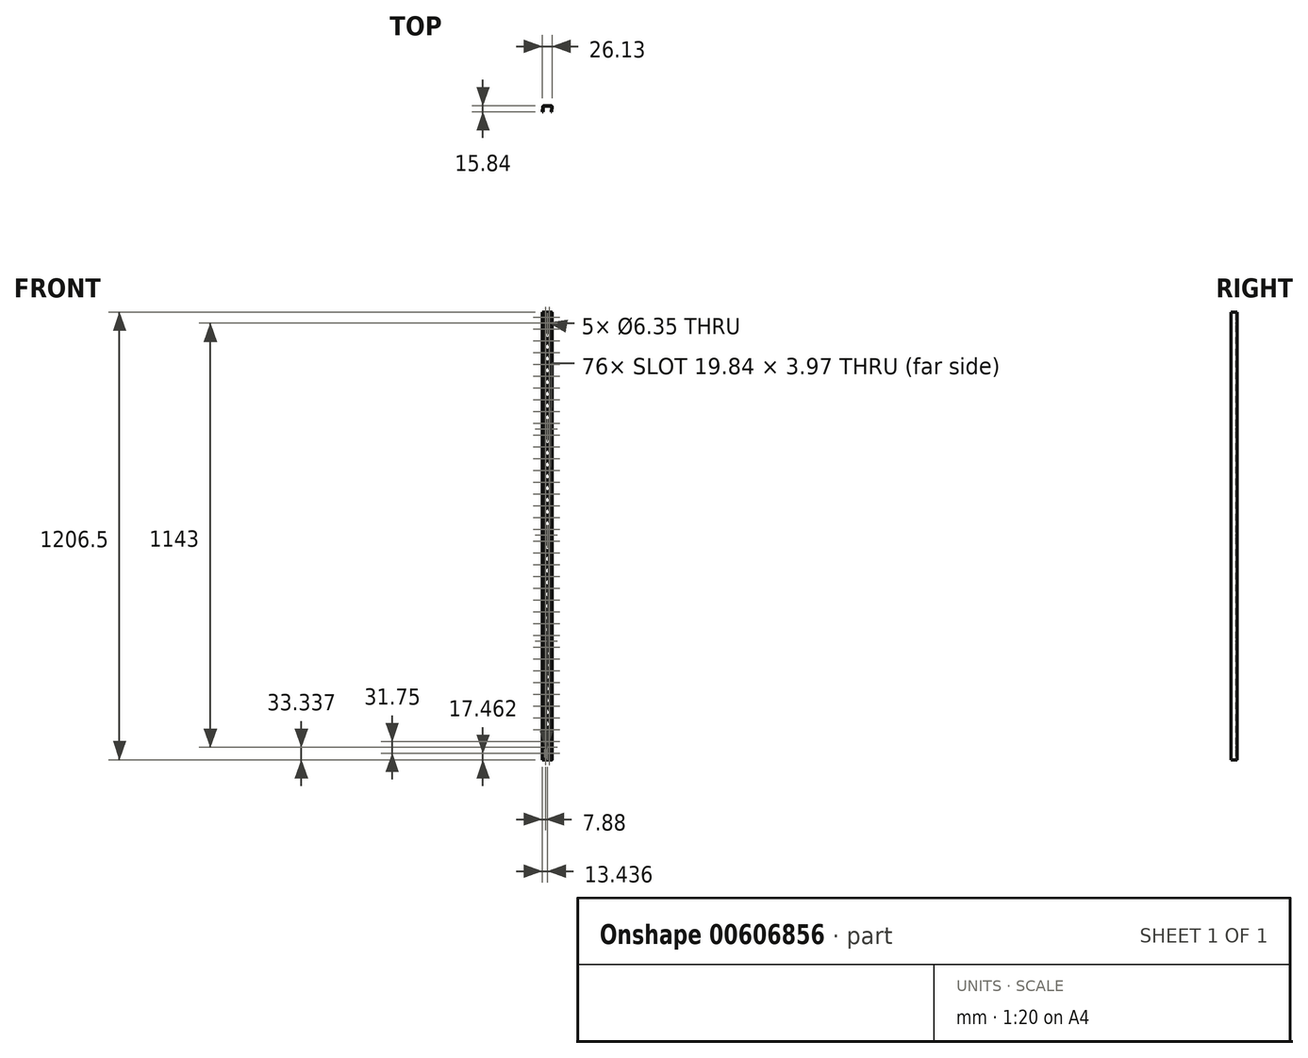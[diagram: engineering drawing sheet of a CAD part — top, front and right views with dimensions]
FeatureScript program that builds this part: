
annotation { "Feature Type Name" : "Feature", "Feature Type Description" : "" }
export const myFeature = defineFeature(function(context is Context, id is Id, definition is map)
    precondition{}
    {
        {
            var Q0;
            Q0=qCreatedBy(makeId("Top.planeOp"),FACE);
            var sketch = newSketch(context, id + "F0", { "sketchPlane" : qUnion([Q0])});
            skLineSegment(sketch, "E0.bottom", {"start": v(9.77, 7.92) * mm, "end": v(-9.22, 7.92) * mm});
            skLineSegment(sketch, "E0.left", {"start": v(12.97, 4.54) * mm, "end": v(12.24, -7.92) * mm});
            skLineSegment(sketch, "E0.right", {"start": v(-12.41, 4.91) * mm, "end": v(-13.16, -7.92) * mm});
            skPoint(sketch, "E0.middle", {"position": v(0, 0) * mm});
            skLineSegment(sketch, "E1.0", {"start": v(11.38, 4.64) * mm, "end": v(10.65, -7.92) * mm});
            skLineSegment(sketch, "E1.1", {"start": v(9.78, 6.34) * mm, "end": v(-9.23, 6.34) * mm});
            skLineSegment(sketch, "E1.2", {"start": v(-10.83, 4.83) * mm, "end": v(-11.57, -7.92) * mm});
            skPoint(sketch, "E2.visualSharp", {"position": v(-10.74, 6.34) * mm});
            skArc(sketch, "E2.filletArc", {"start": v(-9.23, 6.34) * mm, "mid": v(-10.33, 5.9) * mm, "end": v(-10.83, 4.83) * mm});
            skPoint(sketch, "E3.visualSharp", {"position": v(11.48, 6.34) * mm});
            skArc(sketch, "E3.filletArc", {"start": v(11.38, 4.64) * mm, "mid": v(10.95, 5.83) * mm, "end": v(9.78, 6.34) * mm});
            skLineSegment(sketch, "E4", {"start": v(10.65, -7.92) * mm, "end": v(12.24, -7.92) * mm});
            skPoint(sketch, "E5.visualSharp", {"position": v(-12.24, 7.92) * mm});
            skArc(sketch, "E5.filletArc", {"start": v(-9.22, 7.92) * mm, "mid": v(-11.41, 7.05) * mm, "end": v(-12.41, 4.91) * mm});
            skPoint(sketch, "E6.visualSharp", {"position": v(13.16, 7.92) * mm});
            skArc(sketch, "E6.filletArc", {"start": v(12.97, 4.54) * mm, "mid": v(12.1, 6.92) * mm, "end": v(9.77, 7.92) * mm});
            skLineSegment(sketch, "E7", {"start": v(-11.57, -7.92) * mm, "end": v(-13.16, -7.92) * mm});
            skSolve(sketch);
        }
        {
            var Q0;
            Q0 = qSketchRegion(id + "F0", true);
            extrude(context, id + "F1", {"entities" : qUnion([Q0]), "depth" : 1206.5 * mm, "offsetDistance" : 25.4 * mm});
        }
        {
            var Q0;
            Q0=makeQuery(id+"F1.opExtrude","SWEPT_FACE",FACE,{"disambiguationData":[OSD([sQuery(id+"F0.wireOp",EDGE,"E0.bottom")])]});
            var sketch = newSketch(context, id + "F2", { "sketchPlane" : qUnion([Q0])});
            skCircle(sketch, "E8", {"center": v(-0.28, 33.34) * mm, "radius": 3.18 * mm});
            skPoint(sketch, "E8.centerSnap0", {"position": v(-0.28, 0) * mm});
            skCircle(sketch, "E9.0.1.0", {"center": v(-0.28, 319.09) * mm, "radius": 3.18 * mm});
            skCircle(sketch, "E9.0.2.0", {"center": v(-0.28, 604.84) * mm, "radius": 3.18 * mm});
            skCircle(sketch, "E9.0.3.0", {"center": v(-0.28, 890.59) * mm, "radius": 3.18 * mm});
            skCircle(sketch, "E9.0.4.0", {"center": v(-0.28, 1176.34) * mm, "radius": 3.18 * mm});
            skLineSegment(sketch, "E9.direction1", {"start": v(-0.28, 33.34) * mm, "end": v(25.12, 33.34) * mm, "construction": true});
            skLineSegment(sketch, "E9.direction2", {"start": v(-0.28, 33.34) * mm, "end": v(-0.28, 319.09) * mm, "construction": true});
            skSolve(sketch);
        }
        {
            var Q0;
            Q0=makeQuery(id+"F2.imprint","IMPRINT",FACE,{"disambiguationData":[TD([[makeQuery(id+"F2.imprint","IMPRINT",EDGE,{"derivedFrom":sQuery(id+"F2.wireOp",EDGE,"E8")}),1.0]])]});
            var Q1;
            Q1=makeQuery(id+"F2.imprint","IMPRINT",FACE,{"disambiguationData":[TD([[makeQuery(id+"F2.imprint","IMPRINT",EDGE,{"derivedFrom":sQuery(id+"F2.wireOp",EDGE,"E9.0.1.0")}),1.0]])]});
            var Q2;
            Q2=makeQuery(id+"F2.imprint","IMPRINT",FACE,{"disambiguationData":[TD([[makeQuery(id+"F2.imprint","IMPRINT",EDGE,{"derivedFrom":sQuery(id+"F2.wireOp",EDGE,"E9.0.2.0")}),1.0]])]});
            var Q3;
            Q3=makeQuery(id+"F2.imprint","IMPRINT",FACE,{"disambiguationData":[TD([[makeQuery(id+"F2.imprint","IMPRINT",EDGE,{"derivedFrom":sQuery(id+"F2.wireOp",EDGE,"E9.0.3.0")}),1.0]])]});
            var Q4;
            Q4=makeQuery(id+"F2.imprint","IMPRINT",FACE,{"disambiguationData":[TD([[makeQuery(id+"F2.imprint","IMPRINT",EDGE,{"derivedFrom":sQuery(id+"F2.wireOp",EDGE,"E9.0.4.0")}),1.0]])]});
            extrude(context, id + "F3", {"entities" : qUnion([Q0, Q1, Q2, Q3, Q4]), "operationType" : NewBodyOperationType.REMOVE, "oppositeDirection" : true, "depth" : 25.4 * mm, "offsetDistance" : 25.4 * mm});
        }
        {
            var Q0;
            Q0=makeQuery(id+"F1.opExtrude","SWEPT_FACE",FACE,{"disambiguationData":[OSD([sQuery(id+"F0.wireOp",EDGE,"E0.bottom")])]});
            var sketch = newSketch(context, id + "F4", { "sketchPlane" : qUnion([Q0])});
            skLineSegment(sketch, "E10", {"start": v(-0.28, 1204.55) * mm, "end": v(-0.28, 1138.18) * mm, "construction": true});
            skPoint(sketch, "E10.startSnap0", {"position": v(-0.28, 1206.5) * mm});
            skLineSegment(sketch, "E11.left", {"start": v(-7.82, 1200.15) * mm, "end": v(-7.82, 1184.27) * mm});
            skLineSegment(sketch, "E11.right", {"start": v(-3.85, 1200.15) * mm, "end": v(-3.85, 1184.27) * mm});
            skArc(sketch, "E12", {"start": v(-3.85, 1200.15) * mm, "mid": v(-5.83, 1202.13) * mm, "end": v(-7.82, 1200.15) * mm});
            skArc(sketch, "E13", {"start": v(-7.82, 1184.27) * mm, "mid": v(-5.83, 1182.3) * mm, "end": v(-3.85, 1184.27) * mm});
            skLineSegment(sketch, "E14.0.1.0", {"start": v(-3.85, 1168.4) * mm, "end": v(-3.85, 1152.53) * mm});
            skArc(sketch, "E14.0.1.1", {"start": v(-7.82, 1152.53) * mm, "mid": v(-5.83, 1150.54) * mm, "end": v(-3.85, 1152.53) * mm});
            skLineSegment(sketch, "E14.0.1.2", {"start": v(-7.82, 1168.4) * mm, "end": v(-7.82, 1152.53) * mm});
            skArc(sketch, "E14.0.1.3", {"start": v(-3.85, 1168.4) * mm, "mid": v(-5.83, 1170.38) * mm, "end": v(-7.82, 1168.4) * mm});
            skLineSegment(sketch, "E14.0.2.0", {"start": v(-3.85, 1136.65) * mm, "end": v(-3.85, 1120.78) * mm});
            skArc(sketch, "E14.0.2.1", {"start": v(-7.82, 1120.78) * mm, "mid": v(-5.83, 1118.8) * mm, "end": v(-3.85, 1120.78) * mm});
            skLineSegment(sketch, "E14.0.2.2", {"start": v(-7.82, 1136.65) * mm, "end": v(-7.82, 1120.78) * mm});
            skArc(sketch, "E14.0.2.3", {"start": v(-3.85, 1136.65) * mm, "mid": v(-5.83, 1138.63) * mm, "end": v(-7.82, 1136.65) * mm});
            skLineSegment(sketch, "E14.0.3.0", {"start": v(-3.85, 1104.9) * mm, "end": v(-3.85, 1089.03) * mm});
            skArc(sketch, "E14.0.3.1", {"start": v(-7.82, 1089.03) * mm, "mid": v(-5.83, 1087.04) * mm, "end": v(-3.85, 1089.03) * mm});
            skLineSegment(sketch, "E14.0.3.2", {"start": v(-7.82, 1104.9) * mm, "end": v(-7.82, 1089.03) * mm});
            skArc(sketch, "E14.0.3.3", {"start": v(-3.85, 1104.9) * mm, "mid": v(-5.83, 1106.88) * mm, "end": v(-7.82, 1104.9) * mm});
            skLineSegment(sketch, "E14.0.4.0", {"start": v(-3.85, 1073.15) * mm, "end": v(-3.85, 1057.28) * mm});
            skArc(sketch, "E14.0.4.1", {"start": v(-7.82, 1057.28) * mm, "mid": v(-5.83, 1055.3) * mm, "end": v(-3.85, 1057.28) * mm});
            skLineSegment(sketch, "E14.0.4.2", {"start": v(-7.82, 1073.15) * mm, "end": v(-7.82, 1057.28) * mm});
            skArc(sketch, "E14.0.4.3", {"start": v(-3.85, 1073.15) * mm, "mid": v(-5.83, 1075.13) * mm, "end": v(-7.82, 1073.15) * mm});
            skLineSegment(sketch, "E14.0.5.0", {"start": v(-3.85, 1041.4) * mm, "end": v(-3.85, 1025.53) * mm});
            skArc(sketch, "E14.0.5.1", {"start": v(-7.82, 1025.53) * mm, "mid": v(-5.83, 1023.54) * mm, "end": v(-3.85, 1025.53) * mm});
            skLineSegment(sketch, "E14.0.5.2", {"start": v(-7.82, 1041.4) * mm, "end": v(-7.82, 1025.53) * mm});
            skArc(sketch, "E14.0.5.3", {"start": v(-3.85, 1041.4) * mm, "mid": v(-5.83, 1043.38) * mm, "end": v(-7.82, 1041.4) * mm});
            skLineSegment(sketch, "E14.0.6.0", {"start": v(-3.85, 1009.65) * mm, "end": v(-3.85, 993.78) * mm});
            skArc(sketch, "E14.0.6.1", {"start": v(-7.82, 993.78) * mm, "mid": v(-5.83, 991.8) * mm, "end": v(-3.85, 993.78) * mm});
            skLineSegment(sketch, "E14.0.6.2", {"start": v(-7.82, 1009.65) * mm, "end": v(-7.82, 993.78) * mm});
            skArc(sketch, "E14.0.6.3", {"start": v(-3.85, 1009.65) * mm, "mid": v(-5.83, 1011.63) * mm, "end": v(-7.82, 1009.65) * mm});
            skLineSegment(sketch, "E14.0.7.0", {"start": v(-3.85, 977.9) * mm, "end": v(-3.85, 962.03) * mm});
            skArc(sketch, "E14.0.7.1", {"start": v(-7.82, 962.03) * mm, "mid": v(-5.83, 960.04) * mm, "end": v(-3.85, 962.03) * mm});
            skLineSegment(sketch, "E14.0.7.2", {"start": v(-7.82, 977.9) * mm, "end": v(-7.82, 962.03) * mm});
            skArc(sketch, "E14.0.7.3", {"start": v(-3.85, 977.9) * mm, "mid": v(-5.83, 979.88) * mm, "end": v(-7.82, 977.9) * mm});
            skLineSegment(sketch, "E14.0.8.0", {"start": v(-3.85, 946.15) * mm, "end": v(-3.85, 930.28) * mm});
            skArc(sketch, "E14.0.8.1", {"start": v(-7.82, 930.28) * mm, "mid": v(-5.83, 928.3) * mm, "end": v(-3.85, 930.28) * mm});
            skLineSegment(sketch, "E14.0.8.2", {"start": v(-7.82, 946.15) * mm, "end": v(-7.82, 930.28) * mm});
            skArc(sketch, "E14.0.8.3", {"start": v(-3.85, 946.15) * mm, "mid": v(-5.83, 948.13) * mm, "end": v(-7.82, 946.15) * mm});
            skLineSegment(sketch, "E14.0.9.0", {"start": v(-3.85, 914.4) * mm, "end": v(-3.85, 898.53) * mm});
            skArc(sketch, "E14.0.9.1", {"start": v(-7.82, 898.53) * mm, "mid": v(-5.83, 896.54) * mm, "end": v(-3.85, 898.53) * mm});
            skLineSegment(sketch, "E14.0.9.2", {"start": v(-7.82, 914.4) * mm, "end": v(-7.82, 898.53) * mm});
            skArc(sketch, "E14.0.9.3", {"start": v(-3.85, 914.4) * mm, "mid": v(-5.83, 916.38) * mm, "end": v(-7.82, 914.4) * mm});
            skLineSegment(sketch, "E14.0.10.0", {"start": v(-3.85, 882.65) * mm, "end": v(-3.85, 866.78) * mm});
            skArc(sketch, "E14.0.10.1", {"start": v(-7.82, 866.78) * mm, "mid": v(-5.83, 864.8) * mm, "end": v(-3.85, 866.78) * mm});
            skLineSegment(sketch, "E14.0.10.2", {"start": v(-7.82, 882.65) * mm, "end": v(-7.82, 866.78) * mm});
            skArc(sketch, "E14.0.10.3", {"start": v(-3.85, 882.65) * mm, "mid": v(-5.83, 884.63) * mm, "end": v(-7.82, 882.65) * mm});
            skLineSegment(sketch, "E14.0.11.0", {"start": v(-3.85, 850.9) * mm, "end": v(-3.85, 835.03) * mm});
            skArc(sketch, "E14.0.11.1", {"start": v(-7.82, 835.03) * mm, "mid": v(-5.83, 833.04) * mm, "end": v(-3.85, 835.03) * mm});
            skLineSegment(sketch, "E14.0.11.2", {"start": v(-7.82, 850.9) * mm, "end": v(-7.82, 835.03) * mm});
            skArc(sketch, "E14.0.11.3", {"start": v(-3.85, 850.9) * mm, "mid": v(-5.83, 852.88) * mm, "end": v(-7.82, 850.9) * mm});
            skLineSegment(sketch, "E14.0.12.0", {"start": v(-3.85, 819.15) * mm, "end": v(-3.85, 803.28) * mm});
            skArc(sketch, "E14.0.12.1", {"start": v(-7.82, 803.28) * mm, "mid": v(-5.83, 801.3) * mm, "end": v(-3.85, 803.28) * mm});
            skLineSegment(sketch, "E14.0.12.2", {"start": v(-7.82, 819.15) * mm, "end": v(-7.82, 803.28) * mm});
            skArc(sketch, "E14.0.12.3", {"start": v(-3.85, 819.15) * mm, "mid": v(-5.83, 821.13) * mm, "end": v(-7.82, 819.15) * mm});
            skLineSegment(sketch, "E14.0.13.0", {"start": v(-3.85, 787.4) * mm, "end": v(-3.85, 771.53) * mm});
            skArc(sketch, "E14.0.13.1", {"start": v(-7.82, 771.53) * mm, "mid": v(-5.83, 769.54) * mm, "end": v(-3.85, 771.53) * mm});
            skLineSegment(sketch, "E14.0.13.2", {"start": v(-7.82, 787.4) * mm, "end": v(-7.82, 771.53) * mm});
            skArc(sketch, "E14.0.13.3", {"start": v(-3.85, 787.4) * mm, "mid": v(-5.83, 789.38) * mm, "end": v(-7.82, 787.4) * mm});
            skLineSegment(sketch, "E14.0.14.0", {"start": v(-3.85, 755.65) * mm, "end": v(-3.85, 739.78) * mm});
            skArc(sketch, "E14.0.14.1", {"start": v(-7.82, 739.78) * mm, "mid": v(-5.83, 737.8) * mm, "end": v(-3.85, 739.78) * mm});
            skLineSegment(sketch, "E14.0.14.2", {"start": v(-7.82, 755.65) * mm, "end": v(-7.82, 739.78) * mm});
            skArc(sketch, "E14.0.14.3", {"start": v(-3.85, 755.65) * mm, "mid": v(-5.83, 757.63) * mm, "end": v(-7.82, 755.65) * mm});
            skLineSegment(sketch, "E14.0.15.0", {"start": v(-3.85, 723.9) * mm, "end": v(-3.85, 708.03) * mm});
            skArc(sketch, "E14.0.15.1", {"start": v(-7.82, 708.03) * mm, "mid": v(-5.83, 706.04) * mm, "end": v(-3.85, 708.03) * mm});
            skLineSegment(sketch, "E14.0.15.2", {"start": v(-7.82, 723.9) * mm, "end": v(-7.82, 708.03) * mm});
            skArc(sketch, "E14.0.15.3", {"start": v(-3.85, 723.9) * mm, "mid": v(-5.83, 725.88) * mm, "end": v(-7.82, 723.9) * mm});
            skLineSegment(sketch, "E14.0.16.0", {"start": v(-3.85, 692.15) * mm, "end": v(-3.85, 676.28) * mm});
            skArc(sketch, "E14.0.16.1", {"start": v(-7.82, 676.28) * mm, "mid": v(-5.83, 674.3) * mm, "end": v(-3.85, 676.28) * mm});
            skLineSegment(sketch, "E14.0.16.2", {"start": v(-7.82, 692.15) * mm, "end": v(-7.82, 676.28) * mm});
            skArc(sketch, "E14.0.16.3", {"start": v(-3.85, 692.15) * mm, "mid": v(-5.83, 694.13) * mm, "end": v(-7.82, 692.15) * mm});
            skLineSegment(sketch, "E14.0.17.0", {"start": v(-3.85, 660.4) * mm, "end": v(-3.85, 644.53) * mm});
            skArc(sketch, "E14.0.17.1", {"start": v(-7.82, 644.53) * mm, "mid": v(-5.83, 642.54) * mm, "end": v(-3.85, 644.53) * mm});
            skLineSegment(sketch, "E14.0.17.2", {"start": v(-7.82, 660.4) * mm, "end": v(-7.82, 644.53) * mm});
            skArc(sketch, "E14.0.17.3", {"start": v(-3.85, 660.4) * mm, "mid": v(-5.83, 662.38) * mm, "end": v(-7.82, 660.4) * mm});
            skLineSegment(sketch, "E14.0.18.0", {"start": v(-3.85, 628.65) * mm, "end": v(-3.85, 612.78) * mm});
            skArc(sketch, "E14.0.18.1", {"start": v(-7.82, 612.78) * mm, "mid": v(-5.83, 610.8) * mm, "end": v(-3.85, 612.78) * mm});
            skLineSegment(sketch, "E14.0.18.2", {"start": v(-7.82, 628.65) * mm, "end": v(-7.82, 612.78) * mm});
            skArc(sketch, "E14.0.18.3", {"start": v(-3.85, 628.65) * mm, "mid": v(-5.83, 630.63) * mm, "end": v(-7.82, 628.65) * mm});
            skLineSegment(sketch, "E14.0.19.0", {"start": v(-3.85, 596.9) * mm, "end": v(-3.85, 581.03) * mm});
            skArc(sketch, "E14.0.19.1", {"start": v(-7.82, 581.03) * mm, "mid": v(-5.83, 579.04) * mm, "end": v(-3.85, 581.03) * mm});
            skLineSegment(sketch, "E14.0.19.2", {"start": v(-7.82, 596.9) * mm, "end": v(-7.82, 581.03) * mm});
            skArc(sketch, "E14.0.19.3", {"start": v(-3.85, 596.9) * mm, "mid": v(-5.83, 598.88) * mm, "end": v(-7.82, 596.9) * mm});
            skLineSegment(sketch, "E14.0.20.0", {"start": v(-3.85, 565.15) * mm, "end": v(-3.85, 549.28) * mm});
            skArc(sketch, "E14.0.20.1", {"start": v(-7.82, 549.28) * mm, "mid": v(-5.83, 547.3) * mm, "end": v(-3.85, 549.28) * mm});
            skLineSegment(sketch, "E14.0.20.2", {"start": v(-7.82, 565.15) * mm, "end": v(-7.82, 549.28) * mm});
            skArc(sketch, "E14.0.20.3", {"start": v(-3.85, 565.15) * mm, "mid": v(-5.83, 567.13) * mm, "end": v(-7.82, 565.15) * mm});
            skLineSegment(sketch, "E14.0.21.0", {"start": v(-3.85, 533.4) * mm, "end": v(-3.85, 517.53) * mm});
            skArc(sketch, "E14.0.21.1", {"start": v(-7.82, 517.53) * mm, "mid": v(-5.83, 515.54) * mm, "end": v(-3.85, 517.53) * mm});
            skLineSegment(sketch, "E14.0.21.2", {"start": v(-7.82, 533.4) * mm, "end": v(-7.82, 517.53) * mm});
            skArc(sketch, "E14.0.21.3", {"start": v(-3.85, 533.4) * mm, "mid": v(-5.83, 535.38) * mm, "end": v(-7.82, 533.4) * mm});
            skLineSegment(sketch, "E14.0.22.0", {"start": v(-3.85, 501.65) * mm, "end": v(-3.85, 485.78) * mm});
            skArc(sketch, "E14.0.22.1", {"start": v(-7.82, 485.78) * mm, "mid": v(-5.83, 483.8) * mm, "end": v(-3.85, 485.78) * mm});
            skLineSegment(sketch, "E14.0.22.2", {"start": v(-7.82, 501.65) * mm, "end": v(-7.82, 485.78) * mm});
            skArc(sketch, "E14.0.22.3", {"start": v(-3.85, 501.65) * mm, "mid": v(-5.83, 503.63) * mm, "end": v(-7.82, 501.65) * mm});
            skLineSegment(sketch, "E14.0.23.0", {"start": v(-3.85, 469.9) * mm, "end": v(-3.85, 454.03) * mm});
            skArc(sketch, "E14.0.23.1", {"start": v(-7.82, 454.03) * mm, "mid": v(-5.83, 452.04) * mm, "end": v(-3.85, 454.03) * mm});
            skLineSegment(sketch, "E14.0.23.2", {"start": v(-7.82, 469.9) * mm, "end": v(-7.82, 454.03) * mm});
            skArc(sketch, "E14.0.23.3", {"start": v(-3.85, 469.9) * mm, "mid": v(-5.83, 471.88) * mm, "end": v(-7.82, 469.9) * mm});
            skLineSegment(sketch, "E14.0.24.0", {"start": v(-3.85, 438.15) * mm, "end": v(-3.85, 422.28) * mm});
            skArc(sketch, "E14.0.24.1", {"start": v(-7.82, 422.28) * mm, "mid": v(-5.83, 420.3) * mm, "end": v(-3.85, 422.28) * mm});
            skLineSegment(sketch, "E14.0.24.2", {"start": v(-7.82, 438.15) * mm, "end": v(-7.82, 422.28) * mm});
            skArc(sketch, "E14.0.24.3", {"start": v(-3.85, 438.15) * mm, "mid": v(-5.83, 440.13) * mm, "end": v(-7.82, 438.15) * mm});
            skLineSegment(sketch, "E14.0.25.0", {"start": v(-3.85, 406.4) * mm, "end": v(-3.85, 390.53) * mm});
            skArc(sketch, "E14.0.25.1", {"start": v(-7.82, 390.53) * mm, "mid": v(-5.83, 388.54) * mm, "end": v(-3.85, 390.53) * mm});
            skLineSegment(sketch, "E14.0.25.2", {"start": v(-7.82, 406.4) * mm, "end": v(-7.82, 390.53) * mm});
            skArc(sketch, "E14.0.25.3", {"start": v(-3.85, 406.4) * mm, "mid": v(-5.83, 408.38) * mm, "end": v(-7.82, 406.4) * mm});
            skLineSegment(sketch, "E14.0.26.0", {"start": v(-3.85, 374.65) * mm, "end": v(-3.85, 358.78) * mm});
            skArc(sketch, "E14.0.26.1", {"start": v(-7.82, 358.78) * mm, "mid": v(-5.83, 356.8) * mm, "end": v(-3.85, 358.78) * mm});
            skLineSegment(sketch, "E14.0.26.2", {"start": v(-7.82, 374.65) * mm, "end": v(-7.82, 358.78) * mm});
            skArc(sketch, "E14.0.26.3", {"start": v(-3.85, 374.65) * mm, "mid": v(-5.83, 376.63) * mm, "end": v(-7.82, 374.65) * mm});
            skLineSegment(sketch, "E14.0.27.0", {"start": v(-3.85, 342.9) * mm, "end": v(-3.85, 327.03) * mm});
            skArc(sketch, "E14.0.27.1", {"start": v(-7.82, 327.03) * mm, "mid": v(-5.83, 325.04) * mm, "end": v(-3.85, 327.03) * mm});
            skLineSegment(sketch, "E14.0.27.2", {"start": v(-7.82, 342.9) * mm, "end": v(-7.82, 327.03) * mm});
            skArc(sketch, "E14.0.27.3", {"start": v(-3.85, 342.9) * mm, "mid": v(-5.83, 344.88) * mm, "end": v(-7.82, 342.9) * mm});
            skLineSegment(sketch, "E14.0.28.0", {"start": v(-3.85, 311.15) * mm, "end": v(-3.85, 295.28) * mm});
            skArc(sketch, "E14.0.28.1", {"start": v(-7.82, 295.28) * mm, "mid": v(-5.83, 293.3) * mm, "end": v(-3.85, 295.28) * mm});
            skLineSegment(sketch, "E14.0.28.2", {"start": v(-7.82, 311.15) * mm, "end": v(-7.82, 295.28) * mm});
            skArc(sketch, "E14.0.28.3", {"start": v(-3.85, 311.15) * mm, "mid": v(-5.83, 313.13) * mm, "end": v(-7.82, 311.15) * mm});
            skLineSegment(sketch, "E14.0.29.0", {"start": v(-3.85, 279.4) * mm, "end": v(-3.85, 263.53) * mm});
            skArc(sketch, "E14.0.29.1", {"start": v(-7.82, 263.53) * mm, "mid": v(-5.83, 261.54) * mm, "end": v(-3.85, 263.53) * mm});
            skLineSegment(sketch, "E14.0.29.2", {"start": v(-7.82, 279.4) * mm, "end": v(-7.82, 263.53) * mm});
            skArc(sketch, "E14.0.29.3", {"start": v(-3.85, 279.4) * mm, "mid": v(-5.83, 281.38) * mm, "end": v(-7.82, 279.4) * mm});
            skLineSegment(sketch, "E14.0.30.0", {"start": v(-3.85, 247.65) * mm, "end": v(-3.85, 231.78) * mm});
            skArc(sketch, "E14.0.30.1", {"start": v(-7.82, 231.78) * mm, "mid": v(-5.83, 229.8) * mm, "end": v(-3.85, 231.78) * mm});
            skLineSegment(sketch, "E14.0.30.2", {"start": v(-7.82, 247.65) * mm, "end": v(-7.82, 231.78) * mm});
            skArc(sketch, "E14.0.30.3", {"start": v(-3.85, 247.65) * mm, "mid": v(-5.83, 249.63) * mm, "end": v(-7.82, 247.65) * mm});
            skLineSegment(sketch, "E14.0.31.0", {"start": v(-3.85, 215.9) * mm, "end": v(-3.85, 200.03) * mm});
            skArc(sketch, "E14.0.31.1", {"start": v(-7.82, 200.03) * mm, "mid": v(-5.83, 198.04) * mm, "end": v(-3.85, 200.03) * mm});
            skLineSegment(sketch, "E14.0.31.2", {"start": v(-7.82, 215.9) * mm, "end": v(-7.82, 200.03) * mm});
            skArc(sketch, "E14.0.31.3", {"start": v(-3.85, 215.9) * mm, "mid": v(-5.83, 217.88) * mm, "end": v(-7.82, 215.9) * mm});
            skLineSegment(sketch, "E14.0.32.0", {"start": v(-3.85, 184.15) * mm, "end": v(-3.85, 168.28) * mm});
            skArc(sketch, "E14.0.32.1", {"start": v(-7.82, 168.28) * mm, "mid": v(-5.83, 166.3) * mm, "end": v(-3.85, 168.28) * mm});
            skLineSegment(sketch, "E14.0.32.2", {"start": v(-7.82, 184.15) * mm, "end": v(-7.82, 168.28) * mm});
            skArc(sketch, "E14.0.32.3", {"start": v(-3.85, 184.15) * mm, "mid": v(-5.83, 186.13) * mm, "end": v(-7.82, 184.15) * mm});
            skLineSegment(sketch, "E14.0.33.0", {"start": v(-3.85, 152.4) * mm, "end": v(-3.85, 136.53) * mm});
            skArc(sketch, "E14.0.33.1", {"start": v(-7.82, 136.53) * mm, "mid": v(-5.83, 134.54) * mm, "end": v(-3.85, 136.53) * mm});
            skLineSegment(sketch, "E14.0.33.2", {"start": v(-7.82, 152.4) * mm, "end": v(-7.82, 136.53) * mm});
            skArc(sketch, "E14.0.33.3", {"start": v(-3.85, 152.4) * mm, "mid": v(-5.83, 154.38) * mm, "end": v(-7.82, 152.4) * mm});
            skLineSegment(sketch, "E14.0.34.0", {"start": v(-3.85, 120.65) * mm, "end": v(-3.85, 104.78) * mm});
            skArc(sketch, "E14.0.34.1", {"start": v(-7.82, 104.78) * mm, "mid": v(-5.83, 102.8) * mm, "end": v(-3.85, 104.78) * mm});
            skLineSegment(sketch, "E14.0.34.2", {"start": v(-7.82, 120.65) * mm, "end": v(-7.82, 104.78) * mm});
            skArc(sketch, "E14.0.34.3", {"start": v(-3.85, 120.65) * mm, "mid": v(-5.83, 122.63) * mm, "end": v(-7.82, 120.65) * mm});
            skLineSegment(sketch, "E14.0.35.0", {"start": v(-3.85, 88.9) * mm, "end": v(-3.85, 73.03) * mm});
            skArc(sketch, "E14.0.35.1", {"start": v(-7.82, 73.03) * mm, "mid": v(-5.83, 71.04) * mm, "end": v(-3.85, 73.03) * mm});
            skLineSegment(sketch, "E14.0.35.2", {"start": v(-7.82, 88.9) * mm, "end": v(-7.82, 73.03) * mm});
            skArc(sketch, "E14.0.35.3", {"start": v(-3.85, 88.9) * mm, "mid": v(-5.83, 90.88) * mm, "end": v(-7.82, 88.9) * mm});
            skLineSegment(sketch, "E14.0.36.0", {"start": v(-3.85, 57.15) * mm, "end": v(-3.85, 41.28) * mm});
            skArc(sketch, "E14.0.36.1", {"start": v(-7.82, 41.28) * mm, "mid": v(-5.83, 39.3) * mm, "end": v(-3.85, 41.28) * mm});
            skLineSegment(sketch, "E14.0.36.2", {"start": v(-7.82, 57.15) * mm, "end": v(-7.82, 41.28) * mm});
            skArc(sketch, "E14.0.36.3", {"start": v(-3.85, 57.15) * mm, "mid": v(-5.83, 59.13) * mm, "end": v(-7.82, 57.15) * mm});
            skLineSegment(sketch, "E14.0.37.0", {"start": v(-3.85, 25.4) * mm, "end": v(-3.85, 9.53) * mm});
            skArc(sketch, "E14.0.37.1", {"start": v(-7.82, 9.53) * mm, "mid": v(-5.83, 7.54) * mm, "end": v(-3.85, 9.53) * mm});
            skLineSegment(sketch, "E14.0.37.2", {"start": v(-7.82, 25.4) * mm, "end": v(-7.82, 9.53) * mm});
            skArc(sketch, "E14.0.37.3", {"start": v(-3.85, 25.4) * mm, "mid": v(-5.83, 27.38) * mm, "end": v(-7.82, 25.4) * mm});
            skLineSegment(sketch, "E14.1.0.0", {"start": v(7.26, 1200.15) * mm, "end": v(7.26, 1184.27) * mm});
            skArc(sketch, "E14.1.0.1", {"start": v(3.3, 1184.27) * mm, "mid": v(5.28, 1182.3) * mm, "end": v(7.26, 1184.27) * mm});
            skLineSegment(sketch, "E14.1.0.2", {"start": v(3.3, 1200.15) * mm, "end": v(3.3, 1184.27) * mm});
            skArc(sketch, "E14.1.0.3", {"start": v(7.26, 1200.15) * mm, "mid": v(5.28, 1202.13) * mm, "end": v(3.3, 1200.15) * mm});
            skLineSegment(sketch, "E14.1.1.0", {"start": v(7.26, 1168.4) * mm, "end": v(7.26, 1152.53) * mm});
            skArc(sketch, "E14.1.1.1", {"start": v(3.3, 1152.53) * mm, "mid": v(5.28, 1150.54) * mm, "end": v(7.26, 1152.53) * mm});
            skLineSegment(sketch, "E14.1.1.2", {"start": v(3.3, 1168.4) * mm, "end": v(3.3, 1152.53) * mm});
            skArc(sketch, "E14.1.1.3", {"start": v(7.26, 1168.4) * mm, "mid": v(5.28, 1170.38) * mm, "end": v(3.3, 1168.4) * mm});
            skLineSegment(sketch, "E14.1.2.0", {"start": v(7.26, 1136.65) * mm, "end": v(7.26, 1120.78) * mm});
            skArc(sketch, "E14.1.2.1", {"start": v(3.3, 1120.78) * mm, "mid": v(5.28, 1118.8) * mm, "end": v(7.26, 1120.78) * mm});
            skLineSegment(sketch, "E14.1.2.2", {"start": v(3.3, 1136.65) * mm, "end": v(3.3, 1120.78) * mm});
            skArc(sketch, "E14.1.2.3", {"start": v(7.26, 1136.65) * mm, "mid": v(5.28, 1138.63) * mm, "end": v(3.3, 1136.65) * mm});
            skLineSegment(sketch, "E14.1.3.0", {"start": v(7.26, 1104.9) * mm, "end": v(7.26, 1089.03) * mm});
            skArc(sketch, "E14.1.3.1", {"start": v(3.3, 1089.03) * mm, "mid": v(5.28, 1087.04) * mm, "end": v(7.26, 1089.03) * mm});
            skLineSegment(sketch, "E14.1.3.2", {"start": v(3.3, 1104.9) * mm, "end": v(3.3, 1089.03) * mm});
            skArc(sketch, "E14.1.3.3", {"start": v(7.26, 1104.9) * mm, "mid": v(5.28, 1106.88) * mm, "end": v(3.3, 1104.9) * mm});
            skLineSegment(sketch, "E14.1.4.0", {"start": v(7.26, 1073.15) * mm, "end": v(7.26, 1057.28) * mm});
            skArc(sketch, "E14.1.4.1", {"start": v(3.3, 1057.28) * mm, "mid": v(5.28, 1055.3) * mm, "end": v(7.26, 1057.28) * mm});
            skLineSegment(sketch, "E14.1.4.2", {"start": v(3.3, 1073.15) * mm, "end": v(3.3, 1057.28) * mm});
            skArc(sketch, "E14.1.4.3", {"start": v(7.26, 1073.15) * mm, "mid": v(5.28, 1075.13) * mm, "end": v(3.3, 1073.15) * mm});
            skLineSegment(sketch, "E14.1.5.0", {"start": v(7.26, 1041.4) * mm, "end": v(7.26, 1025.53) * mm});
            skArc(sketch, "E14.1.5.1", {"start": v(3.3, 1025.53) * mm, "mid": v(5.28, 1023.54) * mm, "end": v(7.26, 1025.53) * mm});
            skLineSegment(sketch, "E14.1.5.2", {"start": v(3.3, 1041.4) * mm, "end": v(3.3, 1025.53) * mm});
            skArc(sketch, "E14.1.5.3", {"start": v(7.26, 1041.4) * mm, "mid": v(5.28, 1043.38) * mm, "end": v(3.3, 1041.4) * mm});
            skLineSegment(sketch, "E14.1.6.0", {"start": v(7.26, 1009.65) * mm, "end": v(7.26, 993.78) * mm});
            skArc(sketch, "E14.1.6.1", {"start": v(3.3, 993.78) * mm, "mid": v(5.28, 991.8) * mm, "end": v(7.26, 993.78) * mm});
            skLineSegment(sketch, "E14.1.6.2", {"start": v(3.3, 1009.65) * mm, "end": v(3.3, 993.78) * mm});
            skArc(sketch, "E14.1.6.3", {"start": v(7.26, 1009.65) * mm, "mid": v(5.28, 1011.63) * mm, "end": v(3.3, 1009.65) * mm});
            skLineSegment(sketch, "E14.1.7.0", {"start": v(7.26, 977.9) * mm, "end": v(7.26, 962.03) * mm});
            skArc(sketch, "E14.1.7.1", {"start": v(3.3, 962.03) * mm, "mid": v(5.28, 960.04) * mm, "end": v(7.26, 962.03) * mm});
            skLineSegment(sketch, "E14.1.7.2", {"start": v(3.3, 977.9) * mm, "end": v(3.3, 962.03) * mm});
            skArc(sketch, "E14.1.7.3", {"start": v(7.26, 977.9) * mm, "mid": v(5.28, 979.88) * mm, "end": v(3.3, 977.9) * mm});
            skLineSegment(sketch, "E14.1.8.0", {"start": v(7.26, 946.15) * mm, "end": v(7.26, 930.28) * mm});
            skArc(sketch, "E14.1.8.1", {"start": v(3.3, 930.28) * mm, "mid": v(5.28, 928.3) * mm, "end": v(7.26, 930.28) * mm});
            skLineSegment(sketch, "E14.1.8.2", {"start": v(3.3, 946.15) * mm, "end": v(3.3, 930.28) * mm});
            skArc(sketch, "E14.1.8.3", {"start": v(7.26, 946.15) * mm, "mid": v(5.28, 948.13) * mm, "end": v(3.3, 946.15) * mm});
            skLineSegment(sketch, "E14.1.9.0", {"start": v(7.26, 914.4) * mm, "end": v(7.26, 898.53) * mm});
            skArc(sketch, "E14.1.9.1", {"start": v(3.3, 898.53) * mm, "mid": v(5.28, 896.54) * mm, "end": v(7.26, 898.53) * mm});
            skLineSegment(sketch, "E14.1.9.2", {"start": v(3.3, 914.4) * mm, "end": v(3.3, 898.53) * mm});
            skArc(sketch, "E14.1.9.3", {"start": v(7.26, 914.4) * mm, "mid": v(5.28, 916.38) * mm, "end": v(3.3, 914.4) * mm});
            skLineSegment(sketch, "E14.1.10.0", {"start": v(7.26, 882.65) * mm, "end": v(7.26, 866.78) * mm});
            skArc(sketch, "E14.1.10.1", {"start": v(3.3, 866.78) * mm, "mid": v(5.28, 864.8) * mm, "end": v(7.26, 866.78) * mm});
            skLineSegment(sketch, "E14.1.10.2", {"start": v(3.3, 882.65) * mm, "end": v(3.3, 866.78) * mm});
            skArc(sketch, "E14.1.10.3", {"start": v(7.26, 882.65) * mm, "mid": v(5.28, 884.63) * mm, "end": v(3.3, 882.65) * mm});
            skLineSegment(sketch, "E14.1.11.0", {"start": v(7.26, 850.9) * mm, "end": v(7.26, 835.03) * mm});
            skArc(sketch, "E14.1.11.1", {"start": v(3.3, 835.03) * mm, "mid": v(5.28, 833.04) * mm, "end": v(7.26, 835.03) * mm});
            skLineSegment(sketch, "E14.1.11.2", {"start": v(3.3, 850.9) * mm, "end": v(3.3, 835.03) * mm});
            skArc(sketch, "E14.1.11.3", {"start": v(7.26, 850.9) * mm, "mid": v(5.28, 852.88) * mm, "end": v(3.3, 850.9) * mm});
            skLineSegment(sketch, "E14.1.12.0", {"start": v(7.26, 819.15) * mm, "end": v(7.26, 803.28) * mm});
            skArc(sketch, "E14.1.12.1", {"start": v(3.3, 803.28) * mm, "mid": v(5.28, 801.3) * mm, "end": v(7.26, 803.28) * mm});
            skLineSegment(sketch, "E14.1.12.2", {"start": v(3.3, 819.15) * mm, "end": v(3.3, 803.28) * mm});
            skArc(sketch, "E14.1.12.3", {"start": v(7.26, 819.15) * mm, "mid": v(5.28, 821.13) * mm, "end": v(3.3, 819.15) * mm});
            skLineSegment(sketch, "E14.1.13.0", {"start": v(7.26, 787.4) * mm, "end": v(7.26, 771.53) * mm});
            skArc(sketch, "E14.1.13.1", {"start": v(3.3, 771.53) * mm, "mid": v(5.28, 769.54) * mm, "end": v(7.26, 771.53) * mm});
            skLineSegment(sketch, "E14.1.13.2", {"start": v(3.3, 787.4) * mm, "end": v(3.3, 771.53) * mm});
            skArc(sketch, "E14.1.13.3", {"start": v(7.26, 787.4) * mm, "mid": v(5.28, 789.38) * mm, "end": v(3.3, 787.4) * mm});
            skLineSegment(sketch, "E14.1.14.0", {"start": v(7.26, 755.65) * mm, "end": v(7.26, 739.78) * mm});
            skArc(sketch, "E14.1.14.1", {"start": v(3.3, 739.78) * mm, "mid": v(5.28, 737.8) * mm, "end": v(7.26, 739.78) * mm});
            skLineSegment(sketch, "E14.1.14.2", {"start": v(3.3, 755.65) * mm, "end": v(3.3, 739.78) * mm});
            skArc(sketch, "E14.1.14.3", {"start": v(7.26, 755.65) * mm, "mid": v(5.28, 757.63) * mm, "end": v(3.3, 755.65) * mm});
            skLineSegment(sketch, "E14.1.15.0", {"start": v(7.26, 723.9) * mm, "end": v(7.26, 708.03) * mm});
            skArc(sketch, "E14.1.15.1", {"start": v(3.3, 708.03) * mm, "mid": v(5.28, 706.04) * mm, "end": v(7.26, 708.03) * mm});
            skLineSegment(sketch, "E14.1.15.2", {"start": v(3.3, 723.9) * mm, "end": v(3.3, 708.03) * mm});
            skArc(sketch, "E14.1.15.3", {"start": v(7.26, 723.9) * mm, "mid": v(5.28, 725.88) * mm, "end": v(3.3, 723.9) * mm});
            skLineSegment(sketch, "E14.1.16.0", {"start": v(7.26, 692.15) * mm, "end": v(7.26, 676.28) * mm});
            skArc(sketch, "E14.1.16.1", {"start": v(3.3, 676.28) * mm, "mid": v(5.28, 674.3) * mm, "end": v(7.26, 676.28) * mm});
            skLineSegment(sketch, "E14.1.16.2", {"start": v(3.3, 692.15) * mm, "end": v(3.3, 676.28) * mm});
            skArc(sketch, "E14.1.16.3", {"start": v(7.26, 692.15) * mm, "mid": v(5.28, 694.13) * mm, "end": v(3.3, 692.15) * mm});
            skLineSegment(sketch, "E14.1.17.0", {"start": v(7.26, 660.4) * mm, "end": v(7.26, 644.53) * mm});
            skArc(sketch, "E14.1.17.1", {"start": v(3.3, 644.53) * mm, "mid": v(5.28, 642.54) * mm, "end": v(7.26, 644.53) * mm});
            skLineSegment(sketch, "E14.1.17.2", {"start": v(3.3, 660.4) * mm, "end": v(3.3, 644.53) * mm});
            skArc(sketch, "E14.1.17.3", {"start": v(7.26, 660.4) * mm, "mid": v(5.28, 662.38) * mm, "end": v(3.3, 660.4) * mm});
            skLineSegment(sketch, "E14.1.18.0", {"start": v(7.26, 628.65) * mm, "end": v(7.26, 612.78) * mm});
            skArc(sketch, "E14.1.18.1", {"start": v(3.3, 612.78) * mm, "mid": v(5.28, 610.8) * mm, "end": v(7.26, 612.78) * mm});
            skLineSegment(sketch, "E14.1.18.2", {"start": v(3.3, 628.65) * mm, "end": v(3.3, 612.78) * mm});
            skArc(sketch, "E14.1.18.3", {"start": v(7.26, 628.65) * mm, "mid": v(5.28, 630.63) * mm, "end": v(3.3, 628.65) * mm});
            skLineSegment(sketch, "E14.1.19.0", {"start": v(7.26, 596.9) * mm, "end": v(7.26, 581.03) * mm});
            skArc(sketch, "E14.1.19.1", {"start": v(3.3, 581.03) * mm, "mid": v(5.28, 579.04) * mm, "end": v(7.26, 581.03) * mm});
            skLineSegment(sketch, "E14.1.19.2", {"start": v(3.3, 596.9) * mm, "end": v(3.3, 581.03) * mm});
            skArc(sketch, "E14.1.19.3", {"start": v(7.26, 596.9) * mm, "mid": v(5.28, 598.88) * mm, "end": v(3.3, 596.9) * mm});
            skLineSegment(sketch, "E14.1.20.0", {"start": v(7.26, 565.15) * mm, "end": v(7.26, 549.28) * mm});
            skArc(sketch, "E14.1.20.1", {"start": v(3.3, 549.28) * mm, "mid": v(5.28, 547.3) * mm, "end": v(7.26, 549.28) * mm});
            skLineSegment(sketch, "E14.1.20.2", {"start": v(3.3, 565.15) * mm, "end": v(3.3, 549.28) * mm});
            skArc(sketch, "E14.1.20.3", {"start": v(7.26, 565.15) * mm, "mid": v(5.28, 567.13) * mm, "end": v(3.3, 565.15) * mm});
            skLineSegment(sketch, "E14.1.21.0", {"start": v(7.26, 533.4) * mm, "end": v(7.26, 517.53) * mm});
            skArc(sketch, "E14.1.21.1", {"start": v(3.3, 517.53) * mm, "mid": v(5.28, 515.54) * mm, "end": v(7.26, 517.53) * mm});
            skLineSegment(sketch, "E14.1.21.2", {"start": v(3.3, 533.4) * mm, "end": v(3.3, 517.53) * mm});
            skArc(sketch, "E14.1.21.3", {"start": v(7.26, 533.4) * mm, "mid": v(5.28, 535.38) * mm, "end": v(3.3, 533.4) * mm});
            skLineSegment(sketch, "E14.1.22.0", {"start": v(7.26, 501.65) * mm, "end": v(7.26, 485.78) * mm});
            skArc(sketch, "E14.1.22.1", {"start": v(3.3, 485.78) * mm, "mid": v(5.28, 483.8) * mm, "end": v(7.26, 485.78) * mm});
            skLineSegment(sketch, "E14.1.22.2", {"start": v(3.3, 501.65) * mm, "end": v(3.3, 485.78) * mm});
            skArc(sketch, "E14.1.22.3", {"start": v(7.26, 501.65) * mm, "mid": v(5.28, 503.63) * mm, "end": v(3.3, 501.65) * mm});
            skLineSegment(sketch, "E14.1.23.0", {"start": v(7.26, 469.9) * mm, "end": v(7.26, 454.03) * mm});
            skArc(sketch, "E14.1.23.1", {"start": v(3.3, 454.03) * mm, "mid": v(5.28, 452.04) * mm, "end": v(7.26, 454.03) * mm});
            skLineSegment(sketch, "E14.1.23.2", {"start": v(3.3, 469.9) * mm, "end": v(3.3, 454.03) * mm});
            skArc(sketch, "E14.1.23.3", {"start": v(7.26, 469.9) * mm, "mid": v(5.28, 471.88) * mm, "end": v(3.3, 469.9) * mm});
            skLineSegment(sketch, "E14.1.24.0", {"start": v(7.26, 438.15) * mm, "end": v(7.26, 422.28) * mm});
            skArc(sketch, "E14.1.24.1", {"start": v(3.3, 422.28) * mm, "mid": v(5.28, 420.3) * mm, "end": v(7.26, 422.28) * mm});
            skLineSegment(sketch, "E14.1.24.2", {"start": v(3.3, 438.15) * mm, "end": v(3.3, 422.28) * mm});
            skArc(sketch, "E14.1.24.3", {"start": v(7.26, 438.15) * mm, "mid": v(5.28, 440.13) * mm, "end": v(3.3, 438.15) * mm});
            skLineSegment(sketch, "E14.1.25.0", {"start": v(7.26, 406.4) * mm, "end": v(7.26, 390.53) * mm});
            skArc(sketch, "E14.1.25.1", {"start": v(3.3, 390.53) * mm, "mid": v(5.28, 388.54) * mm, "end": v(7.26, 390.53) * mm});
            skLineSegment(sketch, "E14.1.25.2", {"start": v(3.3, 406.4) * mm, "end": v(3.3, 390.53) * mm});
            skArc(sketch, "E14.1.25.3", {"start": v(7.26, 406.4) * mm, "mid": v(5.28, 408.38) * mm, "end": v(3.3, 406.4) * mm});
            skLineSegment(sketch, "E14.1.26.0", {"start": v(7.26, 374.65) * mm, "end": v(7.26, 358.78) * mm});
            skArc(sketch, "E14.1.26.1", {"start": v(3.3, 358.78) * mm, "mid": v(5.28, 356.8) * mm, "end": v(7.26, 358.78) * mm});
            skLineSegment(sketch, "E14.1.26.2", {"start": v(3.3, 374.65) * mm, "end": v(3.3, 358.78) * mm});
            skArc(sketch, "E14.1.26.3", {"start": v(7.26, 374.65) * mm, "mid": v(5.28, 376.63) * mm, "end": v(3.3, 374.65) * mm});
            skLineSegment(sketch, "E14.1.27.0", {"start": v(7.26, 342.9) * mm, "end": v(7.26, 327.03) * mm});
            skArc(sketch, "E14.1.27.1", {"start": v(3.3, 327.03) * mm, "mid": v(5.28, 325.04) * mm, "end": v(7.26, 327.03) * mm});
            skLineSegment(sketch, "E14.1.27.2", {"start": v(3.3, 342.9) * mm, "end": v(3.3, 327.03) * mm});
            skArc(sketch, "E14.1.27.3", {"start": v(7.26, 342.9) * mm, "mid": v(5.28, 344.88) * mm, "end": v(3.3, 342.9) * mm});
            skLineSegment(sketch, "E14.1.28.0", {"start": v(7.26, 311.15) * mm, "end": v(7.26, 295.28) * mm});
            skArc(sketch, "E14.1.28.1", {"start": v(3.3, 295.28) * mm, "mid": v(5.28, 293.3) * mm, "end": v(7.26, 295.28) * mm});
            skLineSegment(sketch, "E14.1.28.2", {"start": v(3.3, 311.15) * mm, "end": v(3.3, 295.28) * mm});
            skArc(sketch, "E14.1.28.3", {"start": v(7.26, 311.15) * mm, "mid": v(5.28, 313.13) * mm, "end": v(3.3, 311.15) * mm});
            skLineSegment(sketch, "E14.1.29.0", {"start": v(7.26, 279.4) * mm, "end": v(7.26, 263.53) * mm});
            skArc(sketch, "E14.1.29.1", {"start": v(3.3, 263.53) * mm, "mid": v(5.28, 261.54) * mm, "end": v(7.26, 263.53) * mm});
            skLineSegment(sketch, "E14.1.29.2", {"start": v(3.3, 279.4) * mm, "end": v(3.3, 263.53) * mm});
            skArc(sketch, "E14.1.29.3", {"start": v(7.26, 279.4) * mm, "mid": v(5.28, 281.38) * mm, "end": v(3.3, 279.4) * mm});
            skLineSegment(sketch, "E14.1.30.0", {"start": v(7.26, 247.65) * mm, "end": v(7.26, 231.78) * mm});
            skArc(sketch, "E14.1.30.1", {"start": v(3.3, 231.78) * mm, "mid": v(5.28, 229.8) * mm, "end": v(7.26, 231.78) * mm});
            skLineSegment(sketch, "E14.1.30.2", {"start": v(3.3, 247.65) * mm, "end": v(3.3, 231.78) * mm});
            skArc(sketch, "E14.1.30.3", {"start": v(7.26, 247.65) * mm, "mid": v(5.28, 249.63) * mm, "end": v(3.3, 247.65) * mm});
            skLineSegment(sketch, "E14.1.31.0", {"start": v(7.26, 215.9) * mm, "end": v(7.26, 200.03) * mm});
            skArc(sketch, "E14.1.31.1", {"start": v(3.3, 200.03) * mm, "mid": v(5.28, 198.04) * mm, "end": v(7.26, 200.03) * mm});
            skLineSegment(sketch, "E14.1.31.2", {"start": v(3.3, 215.9) * mm, "end": v(3.3, 200.03) * mm});
            skArc(sketch, "E14.1.31.3", {"start": v(7.26, 215.9) * mm, "mid": v(5.28, 217.88) * mm, "end": v(3.3, 215.9) * mm});
            skLineSegment(sketch, "E14.1.32.0", {"start": v(7.26, 184.15) * mm, "end": v(7.26, 168.28) * mm});
            skArc(sketch, "E14.1.32.1", {"start": v(3.3, 168.28) * mm, "mid": v(5.28, 166.3) * mm, "end": v(7.26, 168.28) * mm});
            skLineSegment(sketch, "E14.1.32.2", {"start": v(3.3, 184.15) * mm, "end": v(3.3, 168.28) * mm});
            skArc(sketch, "E14.1.32.3", {"start": v(7.26, 184.15) * mm, "mid": v(5.28, 186.13) * mm, "end": v(3.3, 184.15) * mm});
            skLineSegment(sketch, "E14.1.33.0", {"start": v(7.26, 152.4) * mm, "end": v(7.26, 136.53) * mm});
            skArc(sketch, "E14.1.33.1", {"start": v(3.3, 136.53) * mm, "mid": v(5.28, 134.54) * mm, "end": v(7.26, 136.53) * mm});
            skLineSegment(sketch, "E14.1.33.2", {"start": v(3.3, 152.4) * mm, "end": v(3.3, 136.53) * mm});
            skArc(sketch, "E14.1.33.3", {"start": v(7.26, 152.4) * mm, "mid": v(5.28, 154.38) * mm, "end": v(3.3, 152.4) * mm});
            skLineSegment(sketch, "E14.1.34.0", {"start": v(7.26, 120.65) * mm, "end": v(7.26, 104.78) * mm});
            skArc(sketch, "E14.1.34.1", {"start": v(3.3, 104.78) * mm, "mid": v(5.28, 102.8) * mm, "end": v(7.26, 104.78) * mm});
            skLineSegment(sketch, "E14.1.34.2", {"start": v(3.3, 120.65) * mm, "end": v(3.3, 104.78) * mm});
            skArc(sketch, "E14.1.34.3", {"start": v(7.26, 120.65) * mm, "mid": v(5.28, 122.63) * mm, "end": v(3.3, 120.65) * mm});
            skLineSegment(sketch, "E14.1.35.0", {"start": v(7.26, 88.9) * mm, "end": v(7.26, 73.03) * mm});
            skArc(sketch, "E14.1.35.1", {"start": v(3.3, 73.03) * mm, "mid": v(5.28, 71.04) * mm, "end": v(7.26, 73.03) * mm});
            skLineSegment(sketch, "E14.1.35.2", {"start": v(3.3, 88.9) * mm, "end": v(3.3, 73.03) * mm});
            skArc(sketch, "E14.1.35.3", {"start": v(7.26, 88.9) * mm, "mid": v(5.28, 90.88) * mm, "end": v(3.3, 88.9) * mm});
            skLineSegment(sketch, "E14.1.36.0", {"start": v(7.26, 57.15) * mm, "end": v(7.26, 41.28) * mm});
            skArc(sketch, "E14.1.36.1", {"start": v(3.3, 41.28) * mm, "mid": v(5.28, 39.3) * mm, "end": v(7.26, 41.28) * mm});
            skLineSegment(sketch, "E14.1.36.2", {"start": v(3.3, 57.15) * mm, "end": v(3.3, 41.28) * mm});
            skArc(sketch, "E14.1.36.3", {"start": v(7.26, 57.15) * mm, "mid": v(5.28, 59.13) * mm, "end": v(3.3, 57.15) * mm});
            skLineSegment(sketch, "E14.1.37.0", {"start": v(7.26, 25.4) * mm, "end": v(7.26, 9.53) * mm});
            skArc(sketch, "E14.1.37.1", {"start": v(3.3, 9.53) * mm, "mid": v(5.28, 7.54) * mm, "end": v(7.26, 9.53) * mm});
            skLineSegment(sketch, "E14.1.37.2", {"start": v(3.3, 25.4) * mm, "end": v(3.3, 9.53) * mm});
            skArc(sketch, "E14.1.37.3", {"start": v(7.26, 25.4) * mm, "mid": v(5.28, 27.38) * mm, "end": v(3.3, 25.4) * mm});
            skLineSegment(sketch, "E14.direction1", {"start": v(-3.85, 1184.27) * mm, "end": v(7.26, 1184.27) * mm, "construction": true});
            skLineSegment(sketch, "E14.direction2", {"start": v(-3.85, 1184.27) * mm, "end": v(-3.85, 1152.53) * mm, "construction": true});
            skSolve(sketch);
        }
        {
            var Q0;
            Q0=makeQuery(id+"F4.imprint","IMPRINT",FACE,{"disambiguationData":[TD([[makeQuery(id+"F4.imprint","IMPRINT",EDGE,{"derivedFrom":sQuery(id+"F4.wireOp",EDGE,"E11.left")}),1.0]])]});
            var Q1;
            Q1=makeQuery(id+"F4.imprint","IMPRINT",FACE,{"disambiguationData":[TD([[makeQuery(id+"F4.imprint","IMPRINT",EDGE,{"derivedFrom":sQuery(id+"F4.wireOp",EDGE,"E14.1.0.0")}),-1.0]])]});
            var Q2;
            Q2=makeQuery(id+"F4.imprint","IMPRINT",FACE,{"disambiguationData":[TD([[makeQuery(id+"F4.imprint","IMPRINT",EDGE,{"derivedFrom":sQuery(id+"F4.wireOp",EDGE,"E14.0.1.0")}),-1.0]])]});
            var Q3;
            Q3=makeQuery(id+"F4.imprint","IMPRINT",FACE,{"disambiguationData":[TD([[makeQuery(id+"F4.imprint","IMPRINT",EDGE,{"derivedFrom":sQuery(id+"F4.wireOp",EDGE,"E14.1.1.0")}),-1.0]])]});
            var Q4;
            Q4=makeQuery(id+"F4.imprint","IMPRINT",FACE,{"disambiguationData":[TD([[makeQuery(id+"F4.imprint","IMPRINT",EDGE,{"derivedFrom":sQuery(id+"F4.wireOp",EDGE,"E14.0.2.0")}),-1.0]])]});
            var Q5;
            Q5=makeQuery(id+"F4.imprint","IMPRINT",FACE,{"disambiguationData":[TD([[makeQuery(id+"F4.imprint","IMPRINT",EDGE,{"derivedFrom":sQuery(id+"F4.wireOp",EDGE,"E14.1.2.0")}),-1.0]])]});
            var Q6;
            Q6=makeQuery(id+"F4.imprint","IMPRINT",FACE,{"disambiguationData":[TD([[makeQuery(id+"F4.imprint","IMPRINT",EDGE,{"derivedFrom":sQuery(id+"F4.wireOp",EDGE,"E14.0.3.0")}),-1.0]])]});
            var Q7;
            Q7=makeQuery(id+"F4.imprint","IMPRINT",FACE,{"disambiguationData":[TD([[makeQuery(id+"F4.imprint","IMPRINT",EDGE,{"derivedFrom":sQuery(id+"F4.wireOp",EDGE,"E14.1.3.0")}),-1.0]])]});
            var Q8;
            Q8=makeQuery(id+"F4.imprint","IMPRINT",FACE,{"disambiguationData":[TD([[makeQuery(id+"F4.imprint","IMPRINT",EDGE,{"derivedFrom":sQuery(id+"F4.wireOp",EDGE,"E14.0.4.0")}),-1.0]])]});
            var Q9;
            Q9=makeQuery(id+"F4.imprint","IMPRINT",FACE,{"disambiguationData":[TD([[makeQuery(id+"F4.imprint","IMPRINT",EDGE,{"derivedFrom":sQuery(id+"F4.wireOp",EDGE,"E14.1.4.0")}),-1.0]])]});
            var Q10;
            Q10=makeQuery(id+"F4.imprint","IMPRINT",FACE,{"disambiguationData":[TD([[makeQuery(id+"F4.imprint","IMPRINT",EDGE,{"derivedFrom":sQuery(id+"F4.wireOp",EDGE,"E14.0.5.0")}),-1.0]])]});
            var Q11;
            Q11=makeQuery(id+"F4.imprint","IMPRINT",FACE,{"disambiguationData":[TD([[makeQuery(id+"F4.imprint","IMPRINT",EDGE,{"derivedFrom":sQuery(id+"F4.wireOp",EDGE,"E14.1.5.0")}),-1.0]])]});
            var Q12;
            Q12=makeQuery(id+"F4.imprint","IMPRINT",FACE,{"disambiguationData":[TD([[makeQuery(id+"F4.imprint","IMPRINT",EDGE,{"derivedFrom":sQuery(id+"F4.wireOp",EDGE,"E14.0.6.0")}),-1.0]])]});
            var Q13;
            Q13=makeQuery(id+"F4.imprint","IMPRINT",FACE,{"disambiguationData":[TD([[makeQuery(id+"F4.imprint","IMPRINT",EDGE,{"derivedFrom":sQuery(id+"F4.wireOp",EDGE,"E14.1.6.0")}),-1.0]])]});
            var Q14;
            Q14=makeQuery(id+"F4.imprint","IMPRINT",FACE,{"disambiguationData":[TD([[makeQuery(id+"F4.imprint","IMPRINT",EDGE,{"derivedFrom":sQuery(id+"F4.wireOp",EDGE,"E14.0.7.0")}),-1.0]])]});
            var Q15;
            Q15=makeQuery(id+"F4.imprint","IMPRINT",FACE,{"disambiguationData":[TD([[makeQuery(id+"F4.imprint","IMPRINT",EDGE,{"derivedFrom":sQuery(id+"F4.wireOp",EDGE,"E14.1.7.0")}),-1.0]])]});
            var Q16;
            Q16=makeQuery(id+"F4.imprint","IMPRINT",FACE,{"disambiguationData":[TD([[makeQuery(id+"F4.imprint","IMPRINT",EDGE,{"derivedFrom":sQuery(id+"F4.wireOp",EDGE,"E14.1.9.0")}),-1.0]])]});
            var Q17;
            Q17=makeQuery(id+"F4.imprint","IMPRINT",FACE,{"disambiguationData":[TD([[makeQuery(id+"F4.imprint","IMPRINT",EDGE,{"derivedFrom":sQuery(id+"F4.wireOp",EDGE,"E14.0.8.0")}),-1.0]])]});
            var Q18;
            Q18=makeQuery(id+"F4.imprint","IMPRINT",FACE,{"disambiguationData":[TD([[makeQuery(id+"F4.imprint","IMPRINT",EDGE,{"derivedFrom":sQuery(id+"F4.wireOp",EDGE,"E14.0.9.0")}),-1.0]])]});
            var Q19;
            Q19=makeQuery(id+"F4.imprint","IMPRINT",FACE,{"disambiguationData":[TD([[makeQuery(id+"F4.imprint","IMPRINT",EDGE,{"derivedFrom":sQuery(id+"F4.wireOp",EDGE,"E14.1.8.0")}),-1.0]])]});
            var Q20;
            Q20=makeQuery(id+"F4.imprint","IMPRINT",FACE,{"disambiguationData":[TD([[makeQuery(id+"F4.imprint","IMPRINT",EDGE,{"derivedFrom":sQuery(id+"F4.wireOp",EDGE,"E14.1.23.0")}),-1.0]])]});
            var Q21;
            Q21=makeQuery(id+"F4.imprint","IMPRINT",FACE,{"disambiguationData":[TD([[makeQuery(id+"F4.imprint","IMPRINT",EDGE,{"derivedFrom":sQuery(id+"F4.wireOp",EDGE,"E14.0.31.0")}),-1.0]])]});
            var Q22;
            Q22=makeQuery(id+"F4.imprint","IMPRINT",FACE,{"disambiguationData":[TD([[makeQuery(id+"F4.imprint","IMPRINT",EDGE,{"derivedFrom":sQuery(id+"F4.wireOp",EDGE,"E14.1.19.0")}),-1.0]])]});
            var Q23;
            Q23=makeQuery(id+"F4.imprint","IMPRINT",FACE,{"disambiguationData":[TD([[makeQuery(id+"F4.imprint","IMPRINT",EDGE,{"derivedFrom":sQuery(id+"F4.wireOp",EDGE,"E14.1.36.0")}),-1.0]])]});
            var Q24;
            Q24=makeQuery(id+"F4.imprint","IMPRINT",FACE,{"disambiguationData":[TD([[makeQuery(id+"F4.imprint","IMPRINT",EDGE,{"derivedFrom":sQuery(id+"F4.wireOp",EDGE,"E14.0.26.0")}),-1.0]])]});
            var Q25;
            Q25=makeQuery(id+"F4.imprint","IMPRINT",FACE,{"disambiguationData":[TD([[makeQuery(id+"F4.imprint","IMPRINT",EDGE,{"derivedFrom":sQuery(id+"F4.wireOp",EDGE,"E14.0.16.0")}),-1.0]])]});
            var Q26;
            Q26=makeQuery(id+"F4.imprint","IMPRINT",FACE,{"disambiguationData":[TD([[makeQuery(id+"F4.imprint","IMPRINT",EDGE,{"derivedFrom":sQuery(id+"F4.wireOp",EDGE,"E14.1.26.0")}),-1.0]])]});
            var Q27;
            Q27=makeQuery(id+"F4.imprint","IMPRINT",FACE,{"disambiguationData":[TD([[makeQuery(id+"F4.imprint","IMPRINT",EDGE,{"derivedFrom":sQuery(id+"F4.wireOp",EDGE,"E14.0.18.0")}),-1.0]])]});
            var Q28;
            Q28=makeQuery(id+"F4.imprint","IMPRINT",FACE,{"disambiguationData":[TD([[makeQuery(id+"F4.imprint","IMPRINT",EDGE,{"derivedFrom":sQuery(id+"F4.wireOp",EDGE,"E14.1.28.0")}),-1.0]])]});
            var Q29;
            Q29=makeQuery(id+"F4.imprint","IMPRINT",FACE,{"disambiguationData":[TD([[makeQuery(id+"F4.imprint","IMPRINT",EDGE,{"derivedFrom":sQuery(id+"F4.wireOp",EDGE,"E14.1.32.0")}),-1.0]])]});
            var Q30;
            Q30=makeQuery(id+"F4.imprint","IMPRINT",FACE,{"disambiguationData":[TD([[makeQuery(id+"F4.imprint","IMPRINT",EDGE,{"derivedFrom":sQuery(id+"F4.wireOp",EDGE,"E14.0.12.0")}),-1.0]])]});
            var Q31;
            Q31=makeQuery(id+"F4.imprint","IMPRINT",FACE,{"disambiguationData":[TD([[makeQuery(id+"F4.imprint","IMPRINT",EDGE,{"derivedFrom":sQuery(id+"F4.wireOp",EDGE,"E14.1.16.0")}),-1.0]])]});
            var Q32;
            Q32=makeQuery(id+"F4.imprint","IMPRINT",FACE,{"disambiguationData":[TD([[makeQuery(id+"F4.imprint","IMPRINT",EDGE,{"derivedFrom":sQuery(id+"F4.wireOp",EDGE,"E14.0.22.0")}),-1.0]])]});
            var Q33;
            Q33=makeQuery(id+"F4.imprint","IMPRINT",FACE,{"disambiguationData":[TD([[makeQuery(id+"F4.imprint","IMPRINT",EDGE,{"derivedFrom":sQuery(id+"F4.wireOp",EDGE,"E14.1.33.0")}),-1.0]])]});
            var Q34;
            Q34=makeQuery(id+"F4.imprint","IMPRINT",FACE,{"disambiguationData":[TD([[makeQuery(id+"F4.imprint","IMPRINT",EDGE,{"derivedFrom":sQuery(id+"F4.wireOp",EDGE,"E14.1.17.0")}),-1.0]])]});
            var Q35;
            Q35=makeQuery(id+"F4.imprint","IMPRINT",FACE,{"disambiguationData":[TD([[makeQuery(id+"F4.imprint","IMPRINT",EDGE,{"derivedFrom":sQuery(id+"F4.wireOp",EDGE,"E14.0.23.0")}),-1.0]])]});
            var Q36;
            Q36=makeQuery(id+"F4.imprint","IMPRINT",FACE,{"disambiguationData":[TD([[makeQuery(id+"F4.imprint","IMPRINT",EDGE,{"derivedFrom":sQuery(id+"F4.wireOp",EDGE,"E14.1.34.0")}),-1.0]])]});
            var Q37;
            Q37=makeQuery(id+"F4.imprint","IMPRINT",FACE,{"disambiguationData":[TD([[makeQuery(id+"F4.imprint","IMPRINT",EDGE,{"derivedFrom":sQuery(id+"F4.wireOp",EDGE,"E14.1.18.0")}),-1.0]])]});
            var Q38;
            Q38=makeQuery(id+"F4.imprint","IMPRINT",FACE,{"disambiguationData":[TD([[makeQuery(id+"F4.imprint","IMPRINT",EDGE,{"derivedFrom":sQuery(id+"F4.wireOp",EDGE,"E14.0.24.0")}),-1.0]])]});
            var Q39;
            Q39=makeQuery(id+"F4.imprint","IMPRINT",FACE,{"disambiguationData":[TD([[makeQuery(id+"F4.imprint","IMPRINT",EDGE,{"derivedFrom":sQuery(id+"F4.wireOp",EDGE,"E14.1.25.0")}),-1.0]])]});
            var Q40;
            Q40=makeQuery(id+"F4.imprint","IMPRINT",FACE,{"disambiguationData":[TD([[makeQuery(id+"F4.imprint","IMPRINT",EDGE,{"derivedFrom":sQuery(id+"F4.wireOp",EDGE,"E14.1.20.0")}),-1.0]])]});
            var Q41;
            Q41=makeQuery(id+"F4.imprint","IMPRINT",FACE,{"disambiguationData":[TD([[makeQuery(id+"F4.imprint","IMPRINT",EDGE,{"derivedFrom":sQuery(id+"F4.wireOp",EDGE,"E14.0.29.0")}),-1.0]])]});
            var Q42;
            Q42=makeQuery(id+"F4.imprint","IMPRINT",FACE,{"disambiguationData":[TD([[makeQuery(id+"F4.imprint","IMPRINT",EDGE,{"derivedFrom":sQuery(id+"F4.wireOp",EDGE,"E14.1.21.0")}),-1.0]])]});
            var Q43;
            Q43=makeQuery(id+"F4.imprint","IMPRINT",FACE,{"disambiguationData":[TD([[makeQuery(id+"F4.imprint","IMPRINT",EDGE,{"derivedFrom":sQuery(id+"F4.wireOp",EDGE,"E14.0.27.0")}),-1.0]])]});
            var Q44;
            Q44=makeQuery(id+"F4.imprint","IMPRINT",FACE,{"disambiguationData":[TD([[makeQuery(id+"F4.imprint","IMPRINT",EDGE,{"derivedFrom":sQuery(id+"F4.wireOp",EDGE,"E14.0.30.0")}),-1.0]])]});
            var Q45;
            Q45=makeQuery(id+"F4.imprint","IMPRINT",FACE,{"disambiguationData":[TD([[makeQuery(id+"F4.imprint","IMPRINT",EDGE,{"derivedFrom":sQuery(id+"F4.wireOp",EDGE,"E14.1.22.0")}),-1.0]])]});
            var Q46;
            Q46=makeQuery(id+"F4.imprint","IMPRINT",FACE,{"disambiguationData":[TD([[makeQuery(id+"F4.imprint","IMPRINT",EDGE,{"derivedFrom":sQuery(id+"F4.wireOp",EDGE,"E14.0.28.0")}),-1.0]])]});
            var Q47;
            Q47=makeQuery(id+"F4.imprint","IMPRINT",FACE,{"disambiguationData":[TD([[makeQuery(id+"F4.imprint","IMPRINT",EDGE,{"derivedFrom":sQuery(id+"F4.wireOp",EDGE,"E14.0.32.0")}),-1.0]])]});
            var Q48;
            Q48=makeQuery(id+"F4.imprint","IMPRINT",FACE,{"disambiguationData":[TD([[makeQuery(id+"F4.imprint","IMPRINT",EDGE,{"derivedFrom":sQuery(id+"F4.wireOp",EDGE,"E14.0.33.0")}),-1.0]])]});
            var Q49;
            Q49=makeQuery(id+"F4.imprint","IMPRINT",FACE,{"disambiguationData":[TD([[makeQuery(id+"F4.imprint","IMPRINT",EDGE,{"derivedFrom":sQuery(id+"F4.wireOp",EDGE,"E14.0.17.0")}),-1.0]])]});
            var Q50;
            Q50=makeQuery(id+"F4.imprint","IMPRINT",FACE,{"disambiguationData":[TD([[makeQuery(id+"F4.imprint","IMPRINT",EDGE,{"derivedFrom":sQuery(id+"F4.wireOp",EDGE,"E14.1.11.0")}),-1.0]])]});
            var Q51;
            Q51=makeQuery(id+"F4.imprint","IMPRINT",FACE,{"disambiguationData":[TD([[makeQuery(id+"F4.imprint","IMPRINT",EDGE,{"derivedFrom":sQuery(id+"F4.wireOp",EDGE,"E14.1.12.0")}),-1.0]])]});
            var Q52;
            Q52=makeQuery(id+"F4.imprint","IMPRINT",FACE,{"disambiguationData":[TD([[makeQuery(id+"F4.imprint","IMPRINT",EDGE,{"derivedFrom":sQuery(id+"F4.wireOp",EDGE,"E14.0.35.0")}),-1.0]])]});
            var Q53;
            Q53=makeQuery(id+"F4.imprint","IMPRINT",FACE,{"disambiguationData":[TD([[makeQuery(id+"F4.imprint","IMPRINT",EDGE,{"derivedFrom":sQuery(id+"F4.wireOp",EDGE,"E14.1.29.0")}),-1.0]])]});
            var Q54;
            Q54=makeQuery(id+"F4.imprint","IMPRINT",FACE,{"disambiguationData":[TD([[makeQuery(id+"F4.imprint","IMPRINT",EDGE,{"derivedFrom":sQuery(id+"F4.wireOp",EDGE,"E14.1.13.0")}),-1.0]])]});
            var Q55;
            Q55=makeQuery(id+"F4.imprint","IMPRINT",FACE,{"disambiguationData":[TD([[makeQuery(id+"F4.imprint","IMPRINT",EDGE,{"derivedFrom":sQuery(id+"F4.wireOp",EDGE,"E14.1.30.0")}),-1.0]])]});
            var Q56;
            Q56=makeQuery(id+"F4.imprint","IMPRINT",FACE,{"disambiguationData":[TD([[makeQuery(id+"F4.imprint","IMPRINT",EDGE,{"derivedFrom":sQuery(id+"F4.wireOp",EDGE,"E14.1.14.0")}),-1.0]])]});
            var Q57;
            Q57=makeQuery(id+"F4.imprint","IMPRINT",FACE,{"disambiguationData":[TD([[makeQuery(id+"F4.imprint","IMPRINT",EDGE,{"derivedFrom":sQuery(id+"F4.wireOp",EDGE,"E14.0.36.0")}),-1.0]])]});
            var Q58;
            Q58=makeQuery(id+"F4.imprint","IMPRINT",FACE,{"disambiguationData":[TD([[makeQuery(id+"F4.imprint","IMPRINT",EDGE,{"derivedFrom":sQuery(id+"F4.wireOp",EDGE,"E14.0.20.0")}),-1.0]])]});
            var Q59;
            Q59=makeQuery(id+"F4.imprint","IMPRINT",FACE,{"disambiguationData":[TD([[makeQuery(id+"F4.imprint","IMPRINT",EDGE,{"derivedFrom":sQuery(id+"F4.wireOp",EDGE,"E14.0.21.0")}),-1.0]])]});
            var Q60;
            Q60=makeQuery(id+"F4.imprint","IMPRINT",FACE,{"disambiguationData":[TD([[makeQuery(id+"F4.imprint","IMPRINT",EDGE,{"derivedFrom":sQuery(id+"F4.wireOp",EDGE,"E14.1.15.0")}),-1.0]])]});
            var Q61;
            Q61=makeQuery(id+"F4.imprint","IMPRINT",FACE,{"disambiguationData":[TD([[makeQuery(id+"F4.imprint","IMPRINT",EDGE,{"derivedFrom":sQuery(id+"F4.wireOp",EDGE,"E14.0.13.0")}),-1.0]])]});
            var Q62;
            Q62=makeQuery(id+"F4.imprint","IMPRINT",FACE,{"disambiguationData":[TD([[makeQuery(id+"F4.imprint","IMPRINT",EDGE,{"derivedFrom":sQuery(id+"F4.wireOp",EDGE,"E14.0.37.0")}),-1.0]])]});
            var Q63;
            Q63=makeQuery(id+"F4.imprint","IMPRINT",FACE,{"disambiguationData":[TD([[makeQuery(id+"F4.imprint","IMPRINT",EDGE,{"derivedFrom":sQuery(id+"F4.wireOp",EDGE,"E14.0.34.0")}),-1.0]])]});
            var Q64;
            Q64=makeQuery(id+"F4.imprint","IMPRINT",FACE,{"disambiguationData":[TD([[makeQuery(id+"F4.imprint","IMPRINT",EDGE,{"derivedFrom":sQuery(id+"F4.wireOp",EDGE,"E14.1.35.0")}),-1.0]])]});
            var Q65;
            Q65=makeQuery(id+"F4.imprint","IMPRINT",FACE,{"disambiguationData":[TD([[makeQuery(id+"F4.imprint","IMPRINT",EDGE,{"derivedFrom":sQuery(id+"F4.wireOp",EDGE,"E14.1.37.0")}),-1.0]])]});
            var Q66;
            Q66=makeQuery(id+"F4.imprint","IMPRINT",FACE,{"disambiguationData":[TD([[makeQuery(id+"F4.imprint","IMPRINT",EDGE,{"derivedFrom":sQuery(id+"F4.wireOp",EDGE,"E14.1.31.0")}),-1.0]])]});
            var Q67;
            Q67=makeQuery(id+"F4.imprint","IMPRINT",FACE,{"disambiguationData":[TD([[makeQuery(id+"F4.imprint","IMPRINT",EDGE,{"derivedFrom":sQuery(id+"F4.wireOp",EDGE,"E14.1.27.0")}),-1.0]])]});
            var Q68;
            Q68=makeQuery(id+"F4.imprint","IMPRINT",FACE,{"disambiguationData":[TD([[makeQuery(id+"F4.imprint","IMPRINT",EDGE,{"derivedFrom":sQuery(id+"F4.wireOp",EDGE,"E14.0.25.0")}),-1.0]])]});
            var Q69;
            Q69=makeQuery(id+"F4.imprint","IMPRINT",FACE,{"disambiguationData":[TD([[makeQuery(id+"F4.imprint","IMPRINT",EDGE,{"derivedFrom":sQuery(id+"F4.wireOp",EDGE,"E14.1.24.0")}),-1.0]])]});
            var Q70;
            Q70=makeQuery(id+"F4.imprint","IMPRINT",FACE,{"disambiguationData":[TD([[makeQuery(id+"F4.imprint","IMPRINT",EDGE,{"derivedFrom":sQuery(id+"F4.wireOp",EDGE,"E14.0.19.0")}),-1.0]])]});
            var Q71;
            Q71=makeQuery(id+"F4.imprint","IMPRINT",FACE,{"disambiguationData":[TD([[makeQuery(id+"F4.imprint","IMPRINT",EDGE,{"derivedFrom":sQuery(id+"F4.wireOp",EDGE,"E14.0.14.0")}),-1.0]])]});
            var Q72;
            Q72=makeQuery(id+"F4.imprint","IMPRINT",FACE,{"disambiguationData":[TD([[makeQuery(id+"F4.imprint","IMPRINT",EDGE,{"derivedFrom":sQuery(id+"F4.wireOp",EDGE,"E14.0.15.0")}),-1.0]])]});
            var Q73;
            Q73=makeQuery(id+"F4.imprint","IMPRINT",FACE,{"disambiguationData":[TD([[makeQuery(id+"F4.imprint","IMPRINT",EDGE,{"derivedFrom":sQuery(id+"F4.wireOp",EDGE,"E14.0.11.0")}),-1.0]])]});
            var Q74;
            Q74=makeQuery(id+"F4.imprint","IMPRINT",FACE,{"disambiguationData":[TD([[makeQuery(id+"F4.imprint","IMPRINT",EDGE,{"derivedFrom":sQuery(id+"F4.wireOp",EDGE,"E14.0.10.0")}),-1.0]])]});
            var Q75;
            Q75=makeQuery(id+"F4.imprint","IMPRINT",FACE,{"disambiguationData":[TD([[makeQuery(id+"F4.imprint","IMPRINT",EDGE,{"derivedFrom":sQuery(id+"F4.wireOp",EDGE,"E14.1.10.0")}),-1.0]])]});
            var Q76;
            Q76=makeQuery(id+"F1.opExtrude","SWEPT_FACE",FACE,{"disambiguationData":[OSD([sQuery(id+"F0.wireOp",EDGE,"E1.1")])]});
            extrude(context, id + "F5", {"entities" : qUnion([Q0, Q1, Q2, Q3, Q4, Q5, Q6, Q7, Q8, Q9, Q10, Q11, Q12, Q13, Q14, Q15, Q16, Q17, Q18, Q19, Q20, Q21, Q22, Q23, Q24, Q25, Q26, Q27, Q28, Q29, Q30, Q31, Q32, Q33, Q34, Q35, Q36, Q37, Q38, Q39, Q40, Q41, Q42, Q43, Q44, Q45, Q46, Q47, Q48, Q49, Q50, Q51, Q52, Q53, Q54, Q55, Q56, Q57, Q58, Q59, Q60, Q61, Q62, Q63, Q64, Q65, Q66, Q67, Q68, Q69, Q70, Q71, Q72, Q73, Q74, Q75]), "operationType" : NewBodyOperationType.REMOVE, "endBound" : BoundingType.THROUGH_ALL, "oppositeDirection" : true, "depth" : 25.4 * mm, "endBoundEntityFace" : qUnion([Q76]), "offsetDistance" : 25.4 * mm});
        }
    });
